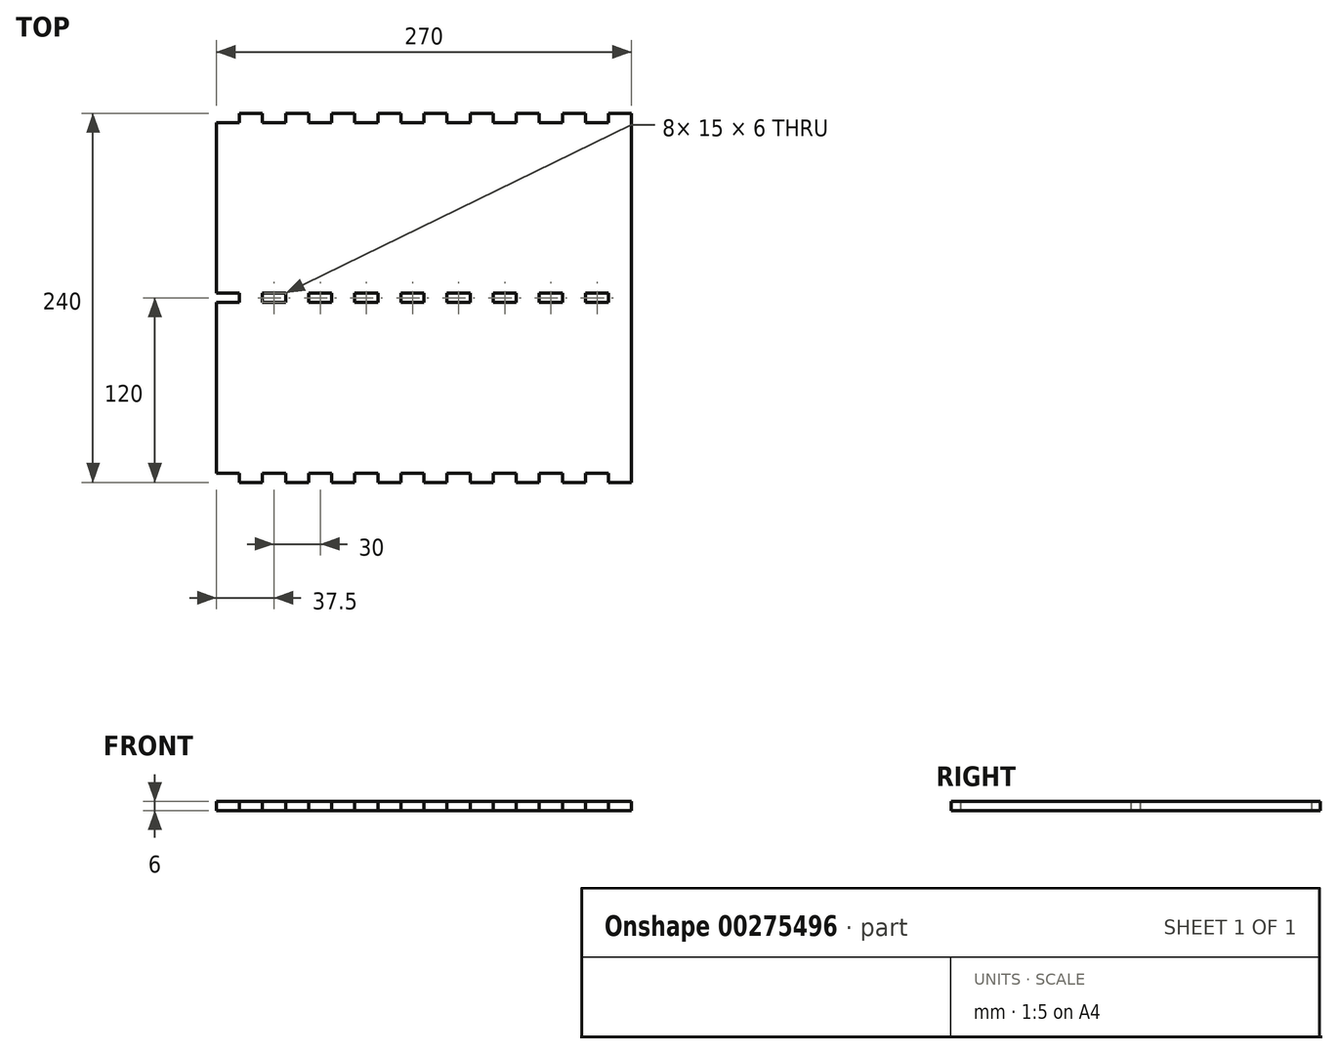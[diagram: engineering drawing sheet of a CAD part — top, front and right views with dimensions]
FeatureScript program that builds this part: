
annotation { "Feature Type Name" : "Feature", "Feature Type Description" : "" }
export const myFeature = defineFeature(function(context is Context, id is Id, definition is map)
    precondition{}
    {
        {
            var Q0;
            Q0=qCreatedBy(makeId("Top.planeOp"),FACE);
            var sketch = newSketch(context, id + "F0", { "sketchPlane" : qUnion([Q0])});
            skLineSegment(sketch, "E0.bottom", {"start": v(15, 0) * mm, "end": v(30, 0) * mm});
            skLineSegment(sketch, "E0.top", {"start": v(15, 240) * mm, "end": v(30, 240) * mm});
            skLineSegment(sketch, "E0.left", {"start": v(0, 0) * mm, "end": v(0, 234) * mm});
            skLineSegment(sketch, "E0.right", {"start": v(270, 0) * mm, "end": v(270, 240) * mm});
            skLineSegment(sketch, "E1.top", {"start": v(0, 234) * mm, "end": v(15, 234) * mm});
            skLineSegment(sketch, "E1.right", {"start": v(15, 240) * mm, "end": v(15, 234) * mm});
            skLineSegment(sketch, "E2.1.0.1", {"start": v(30, 240) * mm, "end": v(30, 234) * mm});
            skLineSegment(sketch, "E2.1.0.2", {"start": v(30, 234) * mm, "end": v(45, 234) * mm});
            skLineSegment(sketch, "E2.1.0.3", {"start": v(45, 240) * mm, "end": v(45, 234) * mm});
            skLineSegment(sketch, "E2.2.0.1", {"start": v(60, 240) * mm, "end": v(60, 234) * mm});
            skLineSegment(sketch, "E2.2.0.2", {"start": v(60, 234) * mm, "end": v(75, 234) * mm});
            skLineSegment(sketch, "E2.2.0.3", {"start": v(75, 240) * mm, "end": v(75, 234) * mm});
            skLineSegment(sketch, "E2.3.0.1", {"start": v(90, 240) * mm, "end": v(90, 234) * mm});
            skLineSegment(sketch, "E2.3.0.2", {"start": v(90, 234) * mm, "end": v(105, 234) * mm});
            skLineSegment(sketch, "E2.3.0.3", {"start": v(105, 240) * mm, "end": v(105, 234) * mm});
            skLineSegment(sketch, "E2.4.0.1", {"start": v(120, 240) * mm, "end": v(120, 234) * mm});
            skLineSegment(sketch, "E2.4.0.2", {"start": v(120, 234) * mm, "end": v(135, 234) * mm});
            skLineSegment(sketch, "E2.4.0.3", {"start": v(135, 240) * mm, "end": v(135, 234) * mm});
            skLineSegment(sketch, "E2.5.0.1", {"start": v(150, 240) * mm, "end": v(150, 234) * mm});
            skLineSegment(sketch, "E2.5.0.2", {"start": v(150, 234) * mm, "end": v(165, 234) * mm});
            skLineSegment(sketch, "E2.5.0.3", {"start": v(165, 240) * mm, "end": v(165, 234) * mm});
            skLineSegment(sketch, "E2.6.0.1", {"start": v(180, 240) * mm, "end": v(180, 234) * mm});
            skLineSegment(sketch, "E2.6.0.2", {"start": v(180, 234) * mm, "end": v(195, 234) * mm});
            skLineSegment(sketch, "E2.6.0.3", {"start": v(195, 240) * mm, "end": v(195, 234) * mm});
            skLineSegment(sketch, "E2.7.0.1", {"start": v(210, 240) * mm, "end": v(210, 234) * mm});
            skLineSegment(sketch, "E2.7.0.2", {"start": v(210, 234) * mm, "end": v(225, 234) * mm});
            skLineSegment(sketch, "E2.7.0.3", {"start": v(225, 240) * mm, "end": v(225, 234) * mm});
            skLineSegment(sketch, "E2.8.0.1", {"start": v(240, 240) * mm, "end": v(240, 234) * mm});
            skLineSegment(sketch, "E2.8.0.2", {"start": v(240, 234) * mm, "end": v(255, 234) * mm});
            skLineSegment(sketch, "E2.8.0.3", {"start": v(255, 240) * mm, "end": v(255, 234) * mm});
            skLineSegment(sketch, "E2.direction1", {"start": v(15, 240) * mm, "end": v(30, 240) * mm, "construction": true});
            skLineSegment(sketch, "E3.trimOffspring", {"start": v(45, 240) * mm, "end": v(60, 240) * mm});
            skLineSegment(sketch, "E4.trimOffspring", {"start": v(75, 240) * mm, "end": v(90, 240) * mm});
            skLineSegment(sketch, "E5.trimOffspring", {"start": v(105, 240) * mm, "end": v(120, 240) * mm});
            skLineSegment(sketch, "E6.trimOffspring", {"start": v(135, 240) * mm, "end": v(150, 240) * mm});
            skLineSegment(sketch, "E7.trimOffspring", {"start": v(165, 240) * mm, "end": v(180, 240) * mm});
            skLineSegment(sketch, "E8.trimOffspring", {"start": v(255, 240) * mm, "end": v(270, 240) * mm});
            skLineSegment(sketch, "E9.trimOffspring", {"start": v(225, 240) * mm, "end": v(240, 240) * mm});
            skLineSegment(sketch, "E10.trimOffspring", {"start": v(195, 240) * mm, "end": v(210, 240) * mm});
            skLineSegment(sketch, "E11.MirrorCS", {"start": v(180, 0) * mm, "end": v(180, 6) * mm});
            skLineSegment(sketch, "E12.MirrorCS", {"start": v(75, 0) * mm, "end": v(75, 6) * mm});
            skLineSegment(sketch, "E13.MirrorCS", {"start": v(90, 0) * mm, "end": v(90, 6) * mm});
            skLineSegment(sketch, "E14.MirrorCS", {"start": v(240, 0) * mm, "end": v(240, 6) * mm});
            skLineSegment(sketch, "E15.MirrorCS", {"start": v(195, 0) * mm, "end": v(195, 6) * mm});
            skLineSegment(sketch, "E16.MirrorCS", {"start": v(210, 0) * mm, "end": v(210, 6) * mm});
            skLineSegment(sketch, "E17.MirrorCS", {"start": v(135, 0) * mm, "end": v(135, 6) * mm});
            skLineSegment(sketch, "E18.MirrorCS", {"start": v(225, 0) * mm, "end": v(225, 6) * mm});
            skLineSegment(sketch, "E19.MirrorCS", {"start": v(15, 0) * mm, "end": v(15, 6) * mm});
            skLineSegment(sketch, "E20.MirrorCS", {"start": v(255, 0) * mm, "end": v(255, 6) * mm});
            skLineSegment(sketch, "E21.MirrorCS", {"start": v(120, 0) * mm, "end": v(120, 6) * mm});
            skLineSegment(sketch, "E22.MirrorCS", {"start": v(165, 0) * mm, "end": v(165, 6) * mm});
            skLineSegment(sketch, "E23.MirrorCS", {"start": v(30, 0) * mm, "end": v(30, 6) * mm});
            skLineSegment(sketch, "E24.MirrorCS", {"start": v(150, 0) * mm, "end": v(150, 6) * mm});
            skLineSegment(sketch, "E25.MirrorCS", {"start": v(45, 0) * mm, "end": v(45, 6) * mm});
            skLineSegment(sketch, "E26.MirrorCS", {"start": v(105, 0) * mm, "end": v(105, 6) * mm});
            skLineSegment(sketch, "E27.MirrorCS", {"start": v(60, 0) * mm, "end": v(60, 6) * mm});
            skLineSegment(sketch, "E28.MirrorCS", {"start": v(135, 0) * mm, "end": v(150, 0) * mm});
            skLineSegment(sketch, "E29.MirrorCS", {"start": v(60, 6) * mm, "end": v(75, 6) * mm});
            skLineSegment(sketch, "E30.MirrorCS", {"start": v(15, 0) * mm, "end": v(30, 0) * mm, "construction": true});
            skLineSegment(sketch, "E31.MirrorCS", {"start": v(120, 6) * mm, "end": v(135, 6) * mm});
            skLineSegment(sketch, "E32.MirrorCS", {"start": v(75, 0) * mm, "end": v(90, 0) * mm});
            skLineSegment(sketch, "E33.MirrorCS", {"start": v(45, 0) * mm, "end": v(60, 0) * mm});
            skLineSegment(sketch, "E34.MirrorCS", {"start": v(225, 0) * mm, "end": v(240, 0) * mm});
            skLineSegment(sketch, "E35.MirrorCS", {"start": v(105, 0) * mm, "end": v(120, 0) * mm});
            skLineSegment(sketch, "E36.MirrorCS", {"start": v(195, 0) * mm, "end": v(210, 0) * mm});
            skLineSegment(sketch, "E37.MirrorCS", {"start": v(0, 6) * mm, "end": v(15, 6) * mm});
            skLineSegment(sketch, "E38.MirrorCS", {"start": v(90, 6) * mm, "end": v(105, 6) * mm});
            skLineSegment(sketch, "E39.MirrorCS", {"start": v(165, 0) * mm, "end": v(180, 0) * mm});
            skLineSegment(sketch, "E40.MirrorCS", {"start": v(180, 6) * mm, "end": v(195, 6) * mm});
            skLineSegment(sketch, "E41.MirrorCS", {"start": v(240, 6) * mm, "end": v(255, 6) * mm});
            skLineSegment(sketch, "E42.MirrorCS", {"start": v(150, 6) * mm, "end": v(165, 6) * mm});
            skLineSegment(sketch, "E43.MirrorCS", {"start": v(210, 6) * mm, "end": v(225, 6) * mm});
            skLineSegment(sketch, "E44.MirrorCS", {"start": v(255, 0) * mm, "end": v(270, 0) * mm});
            skLineSegment(sketch, "E45.MirrorCS", {"start": v(30, 6) * mm, "end": v(45, 6) * mm});
            skSolve(sketch);
        }
        {
            var Q0;
            Q0=makeQuery(id+"F0.imprint","IMPRINT",FACE,{"disambiguationData":[TD([[makeQuery(id+"F0.imprint","IMPRINT",EDGE,{"derivedFrom":sQuery(id+"F0.wireOp",EDGE,"E0.top")}),-1.0]])]});
            extrude(context, id + "F1", {"entities" : qUnion([Q0]), "depth" : 6 * mm});
        }
        {
            var Q0;
            Q0=makeQuery(id+"F1.opExtrude","CAP_FACE",FACE,{"disambiguationData":[OSD([sQuery(id+"F0.wireOp",EDGE,"E0.top"),sQuery(id+"F0.wireOp",EDGE,"E0.left"),sQuery(id+"F0.wireOp",EDGE,"E0.right"),sQuery(id+"F0.wireOp",EDGE,"E1.top"),sQuery(id+"F0.wireOp",EDGE,"E1.right"),sQuery(id+"F0.wireOp",EDGE,"E2.1.0.1"),sQuery(id+"F0.wireOp",EDGE,"E2.1.0.2"),sQuery(id+"F0.wireOp",EDGE,"E2.1.0.3"),sQuery(id+"F0.wireOp",EDGE,"E2.2.0.1"),sQuery(id+"F0.wireOp",EDGE,"E2.2.0.2"),sQuery(id+"F0.wireOp",EDGE,"E2.2.0.3"),sQuery(id+"F0.wireOp",EDGE,"E2.3.0.1"),sQuery(id+"F0.wireOp",EDGE,"E2.3.0.2"),sQuery(id+"F0.wireOp",EDGE,"E2.3.0.3"),sQuery(id+"F0.wireOp",EDGE,"E2.4.0.1"),sQuery(id+"F0.wireOp",EDGE,"E2.4.0.2"),sQuery(id+"F0.wireOp",EDGE,"E2.4.0.3"),sQuery(id+"F0.wireOp",EDGE,"E2.5.0.1"),sQuery(id+"F0.wireOp",EDGE,"E2.5.0.2"),sQuery(id+"F0.wireOp",EDGE,"E2.5.0.3"),sQuery(id+"F0.wireOp",EDGE,"E2.6.0.1"),sQuery(id+"F0.wireOp",EDGE,"E2.6.0.2"),sQuery(id+"F0.wireOp",EDGE,"E2.6.0.3"),sQuery(id+"F0.wireOp",EDGE,"E2.7.0.1"),sQuery(id+"F0.wireOp",EDGE,"E2.7.0.2"),sQuery(id+"F0.wireOp",EDGE,"E2.7.0.3"),sQuery(id+"F0.wireOp",EDGE,"E2.8.0.1"),sQuery(id+"F0.wireOp",EDGE,"E2.8.0.2"),sQuery(id+"F0.wireOp",EDGE,"E2.8.0.3"),sQuery(id+"F0.wireOp",EDGE,"E3.trimOffspring"),sQuery(id+"F0.wireOp",EDGE,"E4.trimOffspring"),sQuery(id+"F0.wireOp",EDGE,"E5.trimOffspring"),sQuery(id+"F0.wireOp",EDGE,"E6.trimOffspring"),sQuery(id+"F0.wireOp",EDGE,"E7.trimOffspring"),sQuery(id+"F0.wireOp",EDGE,"E8.trimOffspring"),sQuery(id+"F0.wireOp",EDGE,"E9.trimOffspring"),sQuery(id+"F0.wireOp",EDGE,"E10.trimOffspring"),sQuery(id+"F0.wireOp",EDGE,"E0.bottom"),sQuery(id+"F0.wireOp",EDGE,"E11.MirrorCS"),sQuery(id+"F0.wireOp",EDGE,"E12.MirrorCS"),sQuery(id+"F0.wireOp",EDGE,"E13.MirrorCS"),sQuery(id+"F0.wireOp",EDGE,"E14.MirrorCS"),sQuery(id+"F0.wireOp",EDGE,"E15.MirrorCS"),sQuery(id+"F0.wireOp",EDGE,"E16.MirrorCS"),sQuery(id+"F0.wireOp",EDGE,"E17.MirrorCS"),sQuery(id+"F0.wireOp",EDGE,"E18.MirrorCS"),sQuery(id+"F0.wireOp",EDGE,"E19.MirrorCS"),sQuery(id+"F0.wireOp",EDGE,"E20.MirrorCS"),sQuery(id+"F0.wireOp",EDGE,"E21.MirrorCS"),sQuery(id+"F0.wireOp",EDGE,"E22.MirrorCS"),sQuery(id+"F0.wireOp",EDGE,"E23.MirrorCS"),sQuery(id+"F0.wireOp",EDGE,"E24.MirrorCS"),sQuery(id+"F0.wireOp",EDGE,"E25.MirrorCS"),sQuery(id+"F0.wireOp",EDGE,"E26.MirrorCS"),sQuery(id+"F0.wireOp",EDGE,"E27.MirrorCS"),sQuery(id+"F0.wireOp",EDGE,"E29.MirrorCS"),sQuery(id+"F0.wireOp",EDGE,"E31.MirrorCS"),sQuery(id+"F0.wireOp",EDGE,"E37.MirrorCS"),sQuery(id+"F0.wireOp",EDGE,"E38.MirrorCS"),sQuery(id+"F0.wireOp",EDGE,"E40.MirrorCS"),sQuery(id+"F0.wireOp",EDGE,"E41.MirrorCS"),sQuery(id+"F0.wireOp",EDGE,"E42.MirrorCS"),sQuery(id+"F0.wireOp",EDGE,"E43.MirrorCS"),sQuery(id+"F0.wireOp",EDGE,"E45.MirrorCS"),sQuery(id+"F0.wireOp",EDGE,"E44.MirrorCS"),sQuery(id+"F0.wireOp",EDGE,"E34.MirrorCS"),sQuery(id+"F0.wireOp",EDGE,"E36.MirrorCS"),sQuery(id+"F0.wireOp",EDGE,"E39.MirrorCS"),sQuery(id+"F0.wireOp",EDGE,"E28.MirrorCS"),sQuery(id+"F0.wireOp",EDGE,"E35.MirrorCS"),sQuery(id+"F0.wireOp",EDGE,"E33.MirrorCS"),sQuery(id+"F0.wireOp",EDGE,"E32.MirrorCS")])],"isStart":false});
            var sketch = newSketch(context, id + "F2", { "sketchPlane" : qUnion([Q0])});
            skLineSegment(sketch, "E46", {"start": v(0, 120) * mm, "end": v(270, 120) * mm});
            skLineSegment(sketch, "E47.bottom", {"start": v(0, 117) * mm, "end": v(15, 117) * mm});
            skLineSegment(sketch, "E47.top", {"start": v(0, 123) * mm, "end": v(15, 123) * mm});
            skLineSegment(sketch, "E47.left", {"start": v(0, 117) * mm, "end": v(0, 123) * mm});
            skLineSegment(sketch, "E47.right", {"start": v(15, 117) * mm, "end": v(15, 123) * mm});
            skLineSegment(sketch, "E48.1.0.0", {"start": v(30, 123) * mm, "end": v(45, 123) * mm});
            skLineSegment(sketch, "E48.1.0.1", {"start": v(45, 117) * mm, "end": v(45, 123) * mm});
            skLineSegment(sketch, "E48.1.0.2", {"start": v(30, 117) * mm, "end": v(45, 117) * mm});
            skLineSegment(sketch, "E48.1.0.3", {"start": v(30, 117) * mm, "end": v(30, 123) * mm});
            skLineSegment(sketch, "E48.2.0.0", {"start": v(60, 123) * mm, "end": v(75, 123) * mm});
            skLineSegment(sketch, "E48.2.0.1", {"start": v(75, 117) * mm, "end": v(75, 123) * mm});
            skLineSegment(sketch, "E48.2.0.2", {"start": v(60, 117) * mm, "end": v(75, 117) * mm});
            skLineSegment(sketch, "E48.2.0.3", {"start": v(60, 117) * mm, "end": v(60, 123) * mm});
            skLineSegment(sketch, "E48.3.0.0", {"start": v(90, 123) * mm, "end": v(105, 123) * mm});
            skLineSegment(sketch, "E48.3.0.1", {"start": v(105, 117) * mm, "end": v(105, 123) * mm});
            skLineSegment(sketch, "E48.3.0.2", {"start": v(90, 117) * mm, "end": v(105, 117) * mm});
            skLineSegment(sketch, "E48.3.0.3", {"start": v(90, 117) * mm, "end": v(90, 123) * mm});
            skLineSegment(sketch, "E48.4.0.0", {"start": v(120, 123) * mm, "end": v(135, 123) * mm});
            skLineSegment(sketch, "E48.4.0.1", {"start": v(135, 117) * mm, "end": v(135, 123) * mm});
            skLineSegment(sketch, "E48.4.0.2", {"start": v(120, 117) * mm, "end": v(135, 117) * mm});
            skLineSegment(sketch, "E48.4.0.3", {"start": v(120, 117) * mm, "end": v(120, 123) * mm});
            skLineSegment(sketch, "E48.5.0.0", {"start": v(150, 123) * mm, "end": v(165, 123) * mm});
            skLineSegment(sketch, "E48.5.0.1", {"start": v(165, 117) * mm, "end": v(165, 123) * mm});
            skLineSegment(sketch, "E48.5.0.2", {"start": v(150, 117) * mm, "end": v(165, 117) * mm});
            skLineSegment(sketch, "E48.5.0.3", {"start": v(150, 117) * mm, "end": v(150, 123) * mm});
            skLineSegment(sketch, "E48.6.0.0", {"start": v(180, 123) * mm, "end": v(195, 123) * mm});
            skLineSegment(sketch, "E48.6.0.1", {"start": v(195, 117) * mm, "end": v(195, 123) * mm});
            skLineSegment(sketch, "E48.6.0.2", {"start": v(180, 117) * mm, "end": v(195, 117) * mm});
            skLineSegment(sketch, "E48.6.0.3", {"start": v(180, 117) * mm, "end": v(180, 123) * mm});
            skLineSegment(sketch, "E48.7.0.0", {"start": v(210, 123) * mm, "end": v(225, 123) * mm});
            skLineSegment(sketch, "E48.7.0.1", {"start": v(225, 117) * mm, "end": v(225, 123) * mm});
            skLineSegment(sketch, "E48.7.0.2", {"start": v(210, 117) * mm, "end": v(225, 117) * mm});
            skLineSegment(sketch, "E48.7.0.3", {"start": v(210, 117) * mm, "end": v(210, 123) * mm});
            skLineSegment(sketch, "E48.8.0.0", {"start": v(240, 123) * mm, "end": v(255, 123) * mm});
            skLineSegment(sketch, "E48.8.0.1", {"start": v(255, 117) * mm, "end": v(255, 123) * mm});
            skLineSegment(sketch, "E48.8.0.2", {"start": v(240, 117) * mm, "end": v(255, 117) * mm});
            skLineSegment(sketch, "E48.8.0.3", {"start": v(240, 117) * mm, "end": v(240, 123) * mm});
            skLineSegment(sketch, "E48.direction1", {"start": v(0, 123) * mm, "end": v(30, 123) * mm, "construction": true});
            skSolve(sketch);
        }
        {
            var Q0;
            {var subQ5=sQuery(id+"F2.wireOp",EDGE,"E47.top");Q0=makeQuery(id+"F2.imprint","IMPRINT",FACE,{"disambiguationData":[TD([[makeQuery(id+"F2.imprint","IMPRINT",EDGE,{"derivedFrom":subQ5}),-1.0]])]});}
            var Q1;
            {var subQ5=sQuery(id+"F2.wireOp",EDGE,"E47.bottom");Q1=makeQuery(id+"F2.imprint","IMPRINT",FACE,{"disambiguationData":[TD([[makeQuery(id+"F2.imprint","IMPRINT",EDGE,{"derivedFrom":subQ5}),1.0]])]});}
            var Q2;
            {var subQ5=sQuery(id+"F2.wireOp",EDGE,"E48.1.0.0");Q2=makeQuery(id+"F2.imprint","IMPRINT",FACE,{"disambiguationData":[TD([[makeQuery(id+"F2.imprint","IMPRINT",EDGE,{"derivedFrom":subQ5}),-1.0]])]});}
            var Q3;
            {var subQ5=sQuery(id+"F2.wireOp",EDGE,"E48.1.0.2");Q3=makeQuery(id+"F2.imprint","IMPRINT",FACE,{"disambiguationData":[TD([[makeQuery(id+"F2.imprint","IMPRINT",EDGE,{"derivedFrom":subQ5}),1.0]])]});}
            var Q4;
            {var subQ5=sQuery(id+"F2.wireOp",EDGE,"E48.2.0.0");Q4=makeQuery(id+"F2.imprint","IMPRINT",FACE,{"disambiguationData":[TD([[makeQuery(id+"F2.imprint","IMPRINT",EDGE,{"derivedFrom":subQ5}),-1.0]])]});}
            var Q5;
            {var subQ5=sQuery(id+"F2.wireOp",EDGE,"E48.2.0.2");Q5=makeQuery(id+"F2.imprint","IMPRINT",FACE,{"disambiguationData":[TD([[makeQuery(id+"F2.imprint","IMPRINT",EDGE,{"derivedFrom":subQ5}),1.0]])]});}
            var Q6;
            {var subQ5=sQuery(id+"F2.wireOp",EDGE,"E48.3.0.0");Q6=makeQuery(id+"F2.imprint","IMPRINT",FACE,{"disambiguationData":[TD([[makeQuery(id+"F2.imprint","IMPRINT",EDGE,{"derivedFrom":subQ5}),-1.0]])]});}
            var Q7;
            {var subQ5=sQuery(id+"F2.wireOp",EDGE,"E48.3.0.2");Q7=makeQuery(id+"F2.imprint","IMPRINT",FACE,{"disambiguationData":[TD([[makeQuery(id+"F2.imprint","IMPRINT",EDGE,{"derivedFrom":subQ5}),1.0]])]});}
            var Q8;
            {var subQ5=sQuery(id+"F2.wireOp",EDGE,"E48.4.0.0");Q8=makeQuery(id+"F2.imprint","IMPRINT",FACE,{"disambiguationData":[TD([[makeQuery(id+"F2.imprint","IMPRINT",EDGE,{"derivedFrom":subQ5}),-1.0]])]});}
            var Q9;
            {var subQ5=sQuery(id+"F2.wireOp",EDGE,"E48.4.0.2");Q9=makeQuery(id+"F2.imprint","IMPRINT",FACE,{"disambiguationData":[TD([[makeQuery(id+"F2.imprint","IMPRINT",EDGE,{"derivedFrom":subQ5}),1.0]])]});}
            var Q10;
            {var subQ5=sQuery(id+"F2.wireOp",EDGE,"E48.5.0.0");Q10=makeQuery(id+"F2.imprint","IMPRINT",FACE,{"disambiguationData":[TD([[makeQuery(id+"F2.imprint","IMPRINT",EDGE,{"derivedFrom":subQ5}),-1.0]])]});}
            var Q11;
            {var subQ5=sQuery(id+"F2.wireOp",EDGE,"E48.5.0.2");Q11=makeQuery(id+"F2.imprint","IMPRINT",FACE,{"disambiguationData":[TD([[makeQuery(id+"F2.imprint","IMPRINT",EDGE,{"derivedFrom":subQ5}),1.0]])]});}
            var Q12;
            {var subQ5=sQuery(id+"F2.wireOp",EDGE,"E48.6.0.0");Q12=makeQuery(id+"F2.imprint","IMPRINT",FACE,{"disambiguationData":[TD([[makeQuery(id+"F2.imprint","IMPRINT",EDGE,{"derivedFrom":subQ5}),-1.0]])]});}
            var Q13;
            {var subQ5=sQuery(id+"F2.wireOp",EDGE,"E48.6.0.2");Q13=makeQuery(id+"F2.imprint","IMPRINT",FACE,{"disambiguationData":[TD([[makeQuery(id+"F2.imprint","IMPRINT",EDGE,{"derivedFrom":subQ5}),1.0]])]});}
            var Q14;
            {var subQ5=sQuery(id+"F2.wireOp",EDGE,"E48.8.0.0");Q14=makeQuery(id+"F2.imprint","IMPRINT",FACE,{"disambiguationData":[TD([[makeQuery(id+"F2.imprint","IMPRINT",EDGE,{"derivedFrom":subQ5}),-1.0]])]});}
            var Q15;
            {var subQ5=sQuery(id+"F2.wireOp",EDGE,"E48.8.0.2");Q15=makeQuery(id+"F2.imprint","IMPRINT",FACE,{"disambiguationData":[TD([[makeQuery(id+"F2.imprint","IMPRINT",EDGE,{"derivedFrom":subQ5}),1.0]])]});}
            var Q16;
            {var subQ5=sQuery(id+"F2.wireOp",EDGE,"E48.7.0.2");Q16=makeQuery(id+"F2.imprint","IMPRINT",FACE,{"disambiguationData":[TD([[makeQuery(id+"F2.imprint","IMPRINT",EDGE,{"derivedFrom":subQ5}),1.0]])]});}
            var Q17;
            {var subQ5=sQuery(id+"F2.wireOp",EDGE,"E48.7.0.0");Q17=makeQuery(id+"F2.imprint","IMPRINT",FACE,{"disambiguationData":[TD([[makeQuery(id+"F2.imprint","IMPRINT",EDGE,{"derivedFrom":subQ5}),-1.0]])]});}
            extrude(context, id + "F3", {"entities" : qUnion([Q0, Q1, Q2, Q3, Q4, Q5, Q6, Q7, Q8, Q9, Q10, Q11, Q12, Q13, Q14, Q15, Q16, Q17]), "operationType" : NewBodyOperationType.REMOVE, "endBound" : BoundingType.THROUGH_ALL, "oppositeDirection" : true, "depth" : 25 * mm});
        }
    });
